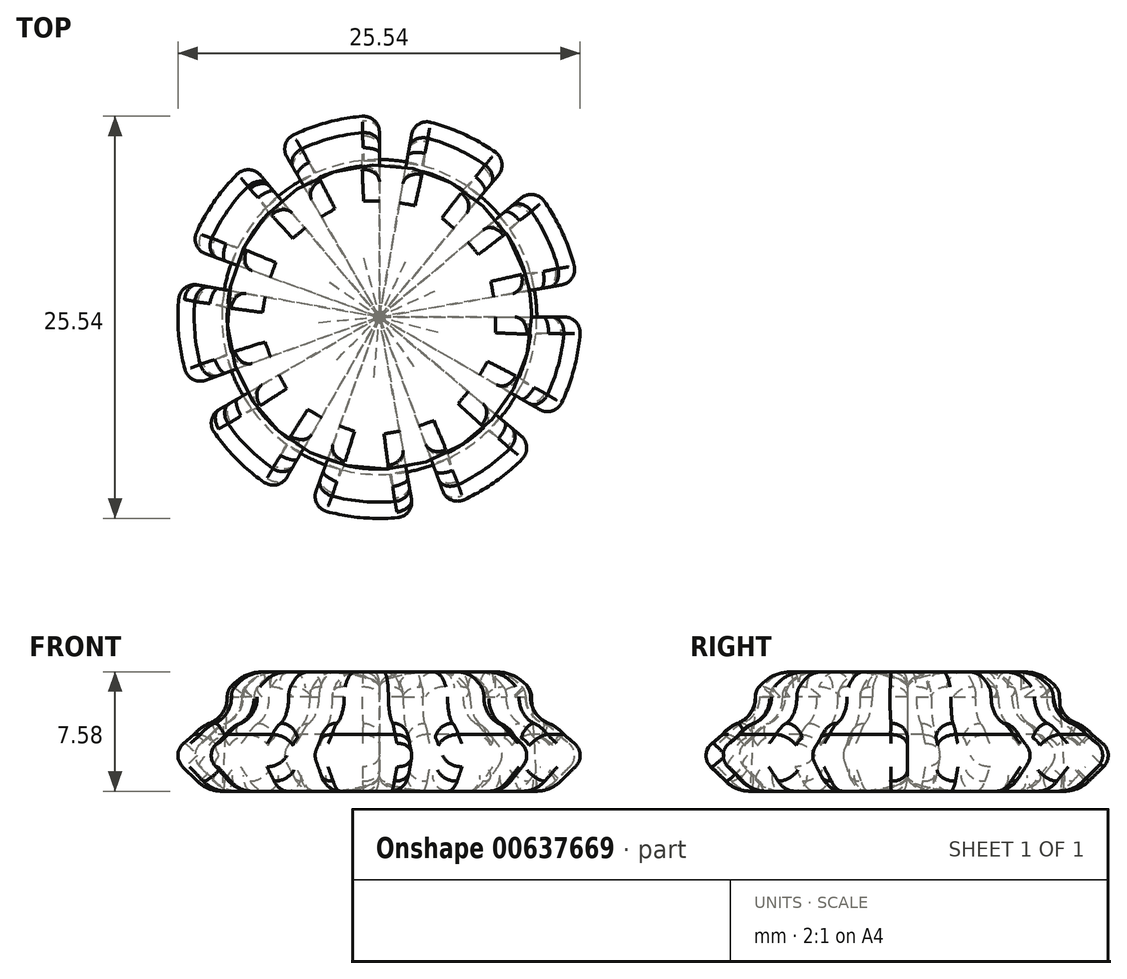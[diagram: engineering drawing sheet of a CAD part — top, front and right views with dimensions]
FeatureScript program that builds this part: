
annotation { "Feature Type Name" : "Feature", "Feature Type Description" : "" }
export const myFeature = defineFeature(function(context is Context, id is Id, definition is map)
    precondition{}
    {
        {
            var Q0;
            Q0=qCreatedBy(makeId("Front.planeOp"),FACE);
            var sketch = newSketch(context, id + "F0", { "sketchPlane" : qUnion([Q0])});
            skLineSegment(sketch, "E0", {"start": v(0, 0) * mm, "end": v(10, 0) * mm});
            skArc(sketch, "E1", {"start": v(10, 0) * mm, "mid": v(12.2, 1.82) * mm, "end": v(10.8, 4.31) * mm});
            skArc(sketch, "E2", {"start": v(9.66, 5.99) * mm, "mid": v(9.6, 6.33) * mm, "end": v(9.43, 6.64) * mm});
            skArc(sketch, "E3", {"start": v(9.66, 5.99) * mm, "mid": v(9.97, 4.97) * mm, "end": v(10.8, 4.31) * mm});
            skLineSegment(sketch, "E4", {"start": v(7.43, 7.58) * mm, "end": v(0, 7.58) * mm});
            skArc(sketch, "E5", {"start": v(9.43, 6.64) * mm, "mid": v(8.54, 7.33) * mm, "end": v(7.43, 7.58) * mm});
            skLineSegment(sketch, "E6", {"start": v(0, 7.58) * mm, "end": v(0, 0) * mm});
            skLineSegment(sketch, "E7", {"start": v(8.66, 6) * mm, "end": v(7.43, 7.58) * mm, "construction": true});
            skLineSegment(sketch, "E8", {"start": v(8.66, 6) * mm, "end": v(10, 2.23) * mm, "construction": true});
            skLineSegment(sketch, "E9", {"start": v(10, 2.23) * mm, "end": v(10, 0) * mm, "construction": true});
            skLineSegment(sketch, "E10", {"start": v(7.43, 4.98) * mm, "end": v(7.43, 7.58) * mm, "construction": true});
            skLineSegment(sketch, "E11", {"start": v(7.43, 4.98) * mm, "end": v(8.66, 6) * mm, "construction": true});
            skLineSegment(sketch, "E12", {"start": v(8.66, 6) * mm, "end": v(11.43, 5.96) * mm, "construction": true});
            skLineSegment(sketch, "E13", {"start": v(11.43, 5.96) * mm, "end": v(10, 2.23) * mm, "construction": true});
            skLineSegment(sketch, "E14", {"start": v(8.66, 6) * mm, "end": v(9.43, 6.64) * mm, "construction": true});
            skLineSegment(sketch, "E15", {"start": v(7.43, 4.98) * mm, "end": v(10, 0) * mm, "construction": true});
            skLineSegment(sketch, "E16", {"start": v(10, 0) * mm, "end": v(9.67, 5.86) * mm});
            skLineSegment(sketch, "E17", {"start": v(11.76, 3.6) * mm, "end": v(13.28, 2.34) * mm});
            skLineSegment(sketch, "E18", {"start": v(13.28, 2.34) * mm, "end": v(11.56, 0.64) * mm});
            skSolve(sketch);
        }
        {
            var Q0;
            Q0 = qSketchRegion(id + "F0", true);
            var Q1;
            Q1=sQuery(id+"F0.wireOp",EDGE,"E6");
            revolve(context, id + "F1", {"entities" : qUnion([Q0]), "axis" : qUnion([Q1]), "revolveType" : RevolveType.ONE_DIRECTION, "angle" : 30 * degree});
        }
        {
            var Q0;
            Q0=makeQuery(id+"F0.imprint","IMPRINT",FACE,{"disambiguationData":[TD([[makeQuery(id+"F0.imprint","IMPRINT",EDGE,{"derivedFrom":sQuery(id+"F0.wireOp",EDGE,"E0")}),1.0]])]});
            var Q1;
            Q1=makeQuery(id+"F1.opRevolve","CAP_EDGE",EDGE,{"disambiguationData":[OSD([sQuery(id+"F0.wireOp",EDGE,"E6")])],"isStart":true});
            revolve(context, id + "F2", {"entities" : qUnion([Q0]), "axis" : qUnion([Q1]), "revolveType" : RevolveType.FULL});
        }
        {
            var Q0;
            Q0=makeQuery(id+"F1.opRevolve","CAP_EDGE",EDGE,{"disambiguationData":[OSD([sQuery(id+"F0.wireOp",EDGE,"E3")])],"isStart":false});
            var Q1;
            {var subQ0=sQuery(id+"F0.wireOp",EDGE,"E1");Q1=makeQuery(id+"F1.opRevolve","CAP_EDGE",EDGE,{"disambiguationData":[OSD([subQ0]),TDD([makeQuery(id+"F0.imprint","IMPRINT",EDGE,{"disambiguationData":[TD([[makeQuery(id+"F0.imprint","INTERSECT",VERTEX,{"derivedFrom":[subQ0,sQuery(id+"F0.wireOp",EDGE,"E3")]}),1.0]])],"derivedFrom":subQ0})])],"isStart":false});}
            var Q2;
            Q2=makeQuery(id+"F1.opRevolve","CAP_EDGE",EDGE,{"disambiguationData":[OSD([sQuery(id+"F0.wireOp",EDGE,"E17")])],"isStart":false});
            var Q3;
            Q3=makeQuery(id+"F1.opRevolve","SWEPT_EDGE",EDGE,{"disambiguationData":[OSD([sQuery(id+"F0.wireOp",EDGE,"E17"),sQuery(id+"F0.wireOp",EDGE,"E18")])]});
            var Q4;
            Q4=makeQuery(id+"F1.opRevolve","CAP_EDGE",EDGE,{"disambiguationData":[OSD([sQuery(id+"F0.wireOp",EDGE,"E18")])],"isStart":false});
            var Q5;
            {var subQ0=sQuery(id+"F0.wireOp",EDGE,"E1");Q5=makeQuery(id+"F1.opRevolve","CAP_EDGE",EDGE,{"disambiguationData":[OSD([subQ0]),TDD([makeQuery(id+"F0.imprint","IMPRINT",EDGE,{"disambiguationData":[TD([[makeQuery(id+"F0.imprint","INTERSECT",VERTEX,{"derivedFrom":[subQ0,sQuery(id+"F0.wireOp",EDGE,"E18")]}),1.0]])],"derivedFrom":subQ0})])],"isStart":false});}
            var Q6;
            Q6=makeQuery(id+"F1.opRevolve","CAP_EDGE",EDGE,{"disambiguationData":[OSD([sQuery(id+"F0.wireOp",EDGE,"E17")])],"isStart":true});
            var Q7;
            {var subQ0=sQuery(id+"F0.wireOp",EDGE,"E1");Q7=makeQuery(id+"F1.opRevolve","CAP_EDGE",EDGE,{"disambiguationData":[OSD([subQ0]),TDD([makeQuery(id+"F0.imprint","IMPRINT",EDGE,{"disambiguationData":[TD([[makeQuery(id+"F0.imprint","INTERSECT",VERTEX,{"derivedFrom":[subQ0,sQuery(id+"F0.wireOp",EDGE,"E3")]}),1.0]])],"derivedFrom":subQ0})])],"isStart":true});}
            var Q8;
            Q8=makeQuery(id+"F1.opRevolve","CAP_EDGE",EDGE,{"disambiguationData":[OSD([sQuery(id+"F0.wireOp",EDGE,"E3")])],"isStart":true});
            var Q9;
            Q9=makeQuery(id+"F1.opRevolve","CAP_EDGE",EDGE,{"disambiguationData":[OSD([sQuery(id+"F0.wireOp",EDGE,"E18")])],"isStart":true});
            var Q10;
            {var subQ0=sQuery(id+"F0.wireOp",EDGE,"E1");Q10=makeQuery(id+"F1.opRevolve","CAP_EDGE",EDGE,{"disambiguationData":[OSD([subQ0]),TDD([makeQuery(id+"F0.imprint","IMPRINT",EDGE,{"disambiguationData":[TD([[makeQuery(id+"F0.imprint","INTERSECT",VERTEX,{"derivedFrom":[subQ0,sQuery(id+"F0.wireOp",EDGE,"E18")]}),1.0]])],"derivedFrom":subQ0})])],"isStart":true});}
            fillet(context, id + "F3", {"entities" : qUnion([Q0, Q1, Q2, Q3, Q4, Q5, Q6, Q7, Q8, Q9, Q10]), "radius" : 1 * mm, "tangentPropagation" : true, "allowEdgeOverflow" : false});
        }
        {
            var Q0;
            Q0=makeQuery(id+"F1.opRevolve","SWEPT_BODY",BODY,{"disambiguationData":[OSD([sQuery(id+"F0.wireOp",EDGE,"E0"),sQuery(id+"F0.wireOp",EDGE,"E1"),sQuery(id+"F0.wireOp",EDGE,"E2"),sQuery(id+"F0.wireOp",EDGE,"E3"),sQuery(id+"F0.wireOp",EDGE,"E4"),sQuery(id+"F0.wireOp",EDGE,"E5"),sQuery(id+"F0.wireOp",EDGE,"E6")])]});
            var Q1;
            Q1=makeQuery(id+"F1.opRevolve","CAP_EDGE",EDGE,{"disambiguationData":[OSD([sQuery(id+"F0.wireOp",EDGE,"E6")])],"isStart":true});
            circularPattern(context, id + "F4", {"entities" : qUnion([Q0]), "axis" : qUnion([Q1]), "angle" : 360 * degree, "instanceCount" : 9, "equalSpace" : true});
        }
    });
